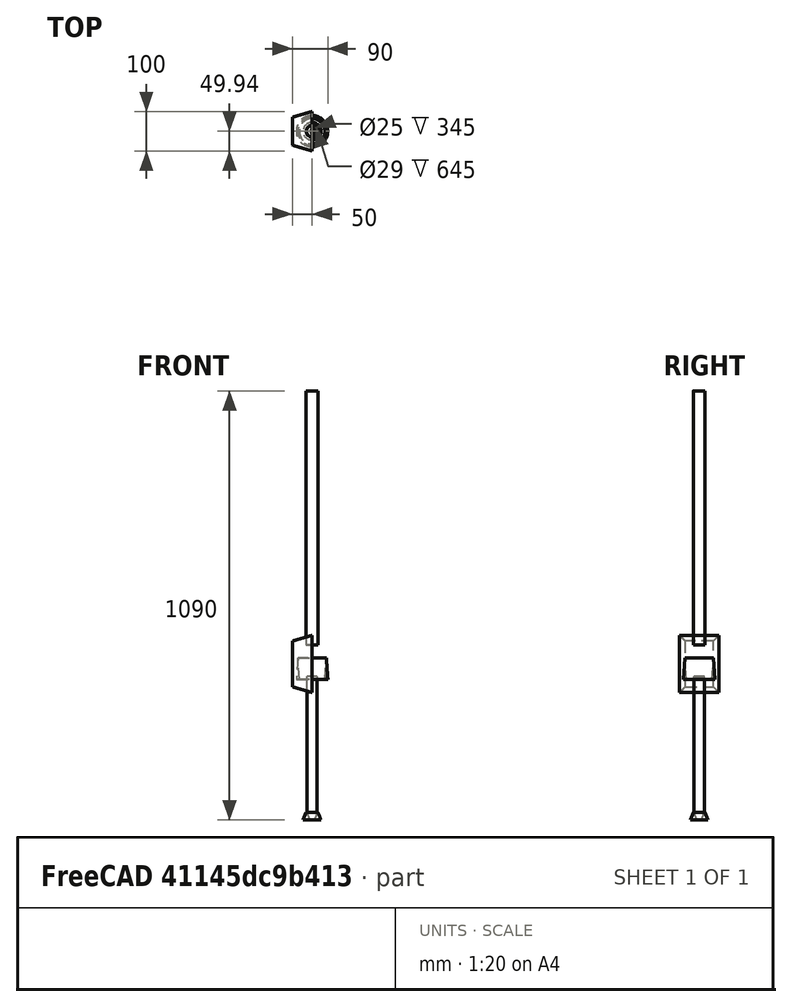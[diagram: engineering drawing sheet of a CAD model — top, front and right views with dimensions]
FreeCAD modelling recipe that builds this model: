
FCSTD DOCUMENT  (FreeCAD 0.21R33771 (Git))
Label: CaneDesign3
License: All rights reserved
LicenseURL: https://en.wikipedia.org/wiki/All_rights_reserved
objects: Sketcher::SketchObject×5, PartDesign::Pad×5, PartDesign::Body×5, Mesh::Feature×2, PartDesign::Plane×1
note: 21 computed .brp shape members not serialized (recipe doc carries the construction recipe); baked Part::Feature solids carry a one-line shape summary decoded from their .brp

FEATURE [Mesh::Feature] ESP_Prototype_v1  label="ESP Prototype v1"
  Placement = pos=(0,0,-40) rot=(0,1,0;0rad)
FEATURE [Sketcher::SketchObject] Sketch
  FullyConstrained = false
  MapMode = 5
  Support = -> [XY_Plane]
  sketch-geometry (2):
    g0: Circle CenterX=0 CenterY=0 CenterZ=0 NormalX=0 NormalY=0 NormalZ=1 AngleXU=0 Radius=15
    g1: Circle CenterX=0 CenterY=0 CenterZ=0 NormalX=0 NormalY=0 NormalZ=1 AngleXU=0 Radius=14.5
  constraints (3):
    c: Coincident(g0,g-1)
    c: Diameter(g0) = 30
    c: Diameter(g1) = 29
FEATURE [PartDesign::Pad] Pad
  Direction = (0,0,1)
  Length = 645
  Length2 = 10
  Profile = -> Sketch
  ReferenceAxis = -> Sketch [N_Axis]
  Type = 0
FEATURE [PartDesign::Body] Body
  Group = -> [Sketch,Pad]
  Origin = -> Origin
  Tip = -> Pad
FEATURE [PartDesign::Plane] DatumPlane
  AttachmentOffset = pos=(0,0,80) rot=(0,0,1;0rad)
  Length = 60
  MapMode = 3
  Placement = pos=(0,1.78e-14,-80) rot=(1,0,0;3.14159rad)
  ResizeMode = 0
  Support = -> [XZ_Plane001]
  Width = 60
FEATURE [Sketcher::SketchObject] Sketch002
  FullyConstrained = false
  MapMode = 5
  Placement = pos=(0,1.78e-14,-80) rot=(1,0,0;3.14159rad)
  Support = -> [DatumPlane]
  sketch-geometry (2):
    g0: Circle CenterX=0 CenterY=0 CenterZ=0 NormalX=0 NormalY=0 NormalZ=1 AngleXU=0 Radius=13
    g1: Circle CenterX=0 CenterY=0 CenterZ=0 NormalX=0 NormalY=0 NormalZ=1 AngleXU=0 Radius=12.5
  constraints (3):
    c: Diameter(g0) = 26
    c: Coincident(g1,g0)
    c: Diameter(g1) = 25
FEATURE [PartDesign::Pad] Pad001
  Direction = (0,2e-16,-1)
  Length = 345
  Length2 = 10
  Placement = pos=(0,1.78e-14,-80) rot=(1,0,0;3.14159rad)
  Profile = -> Sketch002
  ReferenceAxis = -> Sketch002 [N_Axis]
  Type = 0
FEATURE [PartDesign::Body] Body001
  Group = -> [DatumPlane,Sketch002,Pad001]
  Origin = -> Origin001
  Tip = -> Pad001
FEATURE [Sketcher::SketchObject] Sketch003
  FullyConstrained = true
  MapMode = 5
  Placement = pos=(0,0,0) rot=(0.57735,0.57735,0.57735;2.0944rad)
  Support = -> [YZ_Plane002]
  sketch-geometry (4):
    g0: LineSegment StartX=50.0609 StartY=24.0317 StartZ=0 EndX=-49.9391 EndY=24.0317 EndZ=0
    g1: LineSegment StartX=-49.9391 StartY=24.0317 StartZ=0 EndX=-49.9391 EndY=-120.968 EndZ=0
    g2: LineSegment StartX=-49.9391 StartY=-120.968 StartZ=0 EndX=50.0609 EndY=-120.968 EndZ=0
    g3: LineSegment StartX=50.0609 StartY=-120.968 StartZ=0 EndX=50.0609 EndY=24.0317 EndZ=0
  constraints (11):
    c: Coincident(g0,g1)
    c: Coincident(g1,g2)
    c: Coincident(g2,g3)
    c: Coincident(g3,g0)
    c: Horizontal(g0)
    c: Horizontal(g2)
    c: Vertical(g1)
    c: Vertical(g3)
    c: DistanceX(g0,g0) = 100
    c: DistanceY(g3,g3) = 145
    c: Block(g3)
FEATURE [PartDesign::Pad] Pad002
  Direction = (1,-2e-16,3e-16)
  Length = 50
  Length2 = 10
  Placement = pos=(0,0,0) rot=(1,1,1;2.0944rad)
  Profile = -> Sketch003
  ReferenceAxis = -> Sketch003 [N_Axis]
  Reversed = true
  TaperAngle = -15.9
  Type = 0
FEATURE [PartDesign::Body] Body002
  Group = -> [Sketch003,Pad002]
  Origin = -> Origin002
  Tip = -> Pad002
FEATURE [Sketcher::SketchObject] Sketch004
  FullyConstrained = true
  MapMode = 5
  Support = -> [XY_Plane003]
  sketch-geometry (2):
    g0: Circle CenterX=0 CenterY=0 CenterZ=0 NormalX=0 NormalY=0 NormalZ=1 AngleXU=0 Radius=40
    g1: Circle CenterX=0 CenterY=0 CenterZ=0 NormalX=0 NormalY=0 NormalZ=1 AngleXU=0 Radius=32.5
  constraints (4):
    c: Coincident(g0,g-1)
    c: Diameter(g0) = 80
    c: Coincident(g1,g0)
    c: Diameter(g1) = 65
FEATURE [PartDesign::Pad] Pad003
  Direction = (0,0,1)
  Length = 144
  Length2 = 10
  Profile = -> Sketch004
  ReferenceAxis = -> Sketch004 [N_Axis]
  TaperAngle = -3.9
  Type = 0
FEATURE [PartDesign::Body] Body003  label="MotorCover"
  Group = -> [Sketch004,Pad003]
  Origin = -> Origin003
  Placement = pos=(0,0,-88) rot=(0,0,1;0rad)
  Tip = -> Pad003
FEATURE [Sketcher::SketchObject] Sketch005
  FullyConstrained = true
  MapMode = 5
  Support = -> [XY_Plane006]
  sketch-geometry (2):
    g0: Circle CenterX=0 CenterY=0 CenterZ=0 NormalX=0 NormalY=0 NormalZ=1 AngleXU=0 Radius=13.5
    g1: Circle CenterX=0 CenterY=0 CenterZ=0 NormalX=0 NormalY=0 NormalZ=1 AngleXU=0 Radius=15
  constraints (4):
    c: Coincident(g0,g-1)
    c: Diameter(g0) = 27
    c: Coincident(g1,g0)
    c: Diameter(g1) = 30
FEATURE [PartDesign::Pad] Pad005
  Direction = (0,0,1)
  Length = 20
  Length2 = 10
  Profile = -> Sketch005
  ReferenceAxis = -> Sketch005 [N_Axis]
  Reversed = true
  TaperAngle = 21
  Type = 0
FEATURE [PartDesign::Body] Body006  label="Foot"
  Group = -> [Sketch005,Pad005]
  Origin = -> Origin006
  Placement = pos=(0,0,-425) rot=(0,0,1;0rad)
  Tip = -> Pad005
FEATURE [Mesh::Feature] _7097_Cane_flat_handle_v1_NEW  label="17097_Cane_flat_handle_v1_NEW"
  Placement = pos=(-7,4,-36) rot=(0,0,1;3.14159rad)
